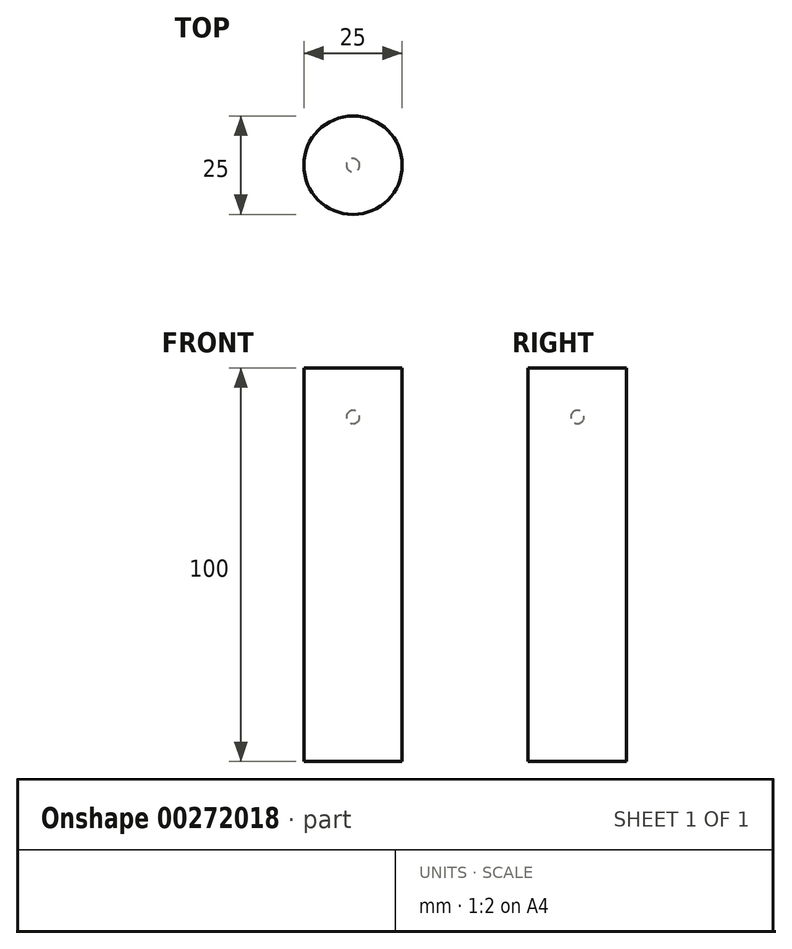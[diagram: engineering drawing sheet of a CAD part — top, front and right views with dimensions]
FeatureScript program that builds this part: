
annotation { "Feature Type Name" : "Feature", "Feature Type Description" : "" }
export const myFeature = defineFeature(function(context is Context, id is Id, definition is map)
    precondition{}
    {
        {
            var Q0;
            Q0=qCreatedBy(makeId("Front.planeOp"),FACE);
            var sketch = newSketch(context, id + "F0", { "sketchPlane" : qUnion([Q0])});
            skLineSegment(sketch, "E0.bottom", {"start": v(6.25, -50) * mm, "end": v(-6.25, -50) * mm});
            skLineSegment(sketch, "E0.top", {"start": v(6.25, 50) * mm, "end": v(-6.25, 50) * mm});
            skLineSegment(sketch, "E0.left", {"start": v(6.25, -50) * mm, "end": v(6.25, 50) * mm});
            skLineSegment(sketch, "E0.right", {"start": v(-6.25, -50) * mm, "end": v(-6.25, 50) * mm});
            skPoint(sketch, "E0.middle", {"position": v(0, 0) * mm});
            skLineSegment(sketch, "E1", {"start": v(-6.25, 50) * mm, "end": v(-6.25, 37.5) * mm, "construction": true});
            skLineSegment(sketch, "E2", {"start": v(-6.25, 37.5) * mm, "end": v(0, 37.5) * mm, "construction": true});
            skCircle(sketch, "E3", {"center": v(-6.25, 37.5) * mm, "radius": 1.69 * mm});
            skSolve(sketch);
        }
        {
            var Q0;
            Q0=sQuery(id+"F0.wireOp",EDGE,"E3");
            extrude(context, id + "F1", {"bodyType" : ToolBodyType.SURFACE, "surfaceEntities" : qUnion([Q0]), "endBound" : BoundingType.SYMMETRIC, "depth" : 30 * mm});
        }
        {
            var Q0;
            Q0 = qSketchRegion(id + "F0", true);
            var Q1;
            Q1=sQuery(id+"F0.wireOp",EDGE,"E0.right");
            revolve(context, id + "F2", {"entities" : qUnion([Q0]), "axis" : qUnion([Q1]), "revolveType" : RevolveType.FULL});
        }
    });
